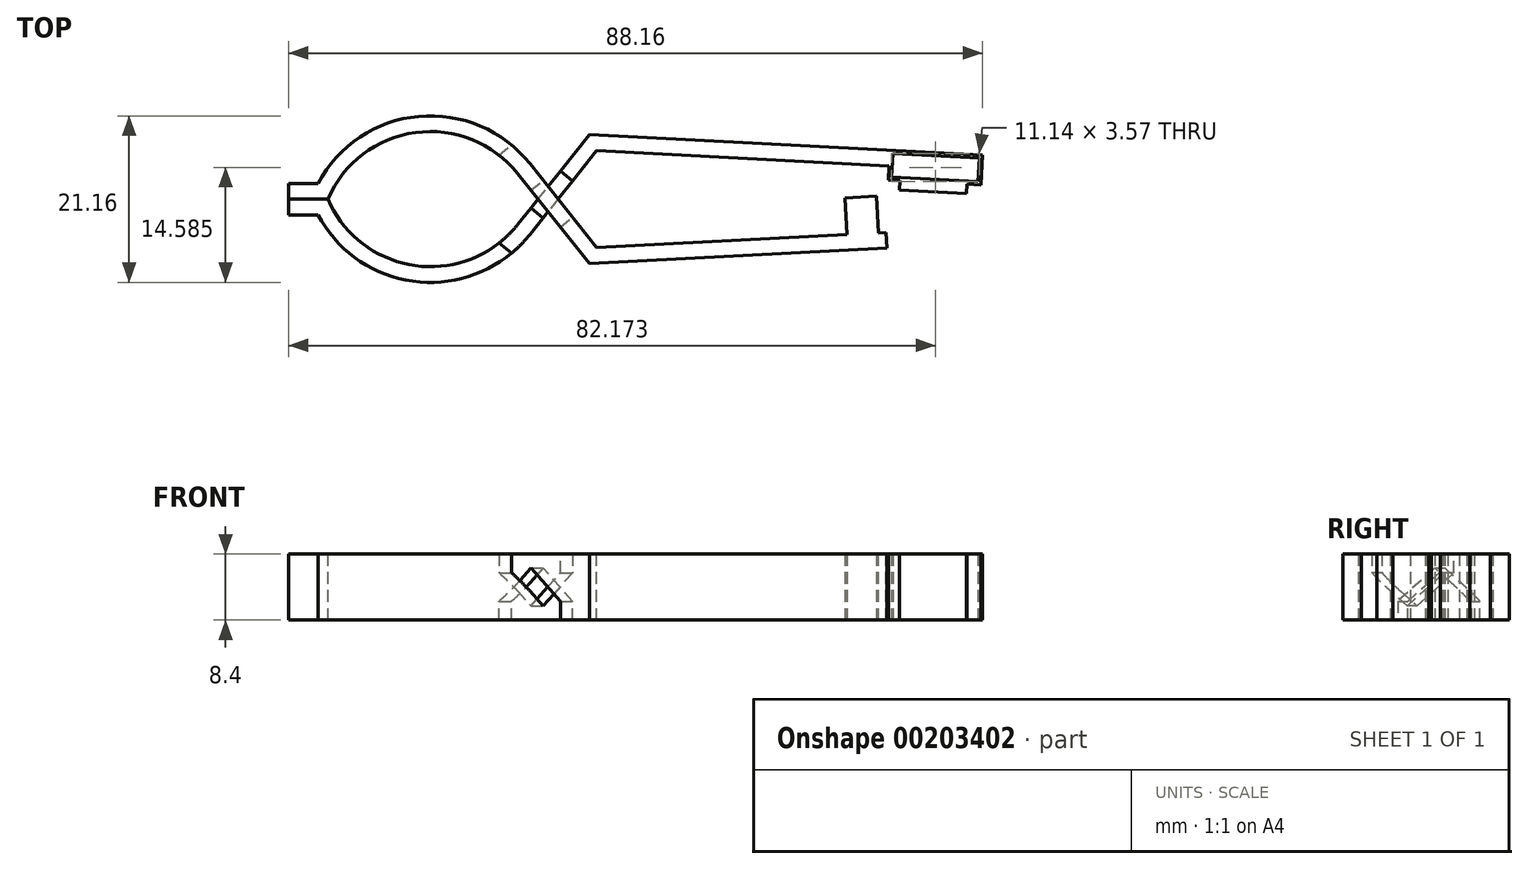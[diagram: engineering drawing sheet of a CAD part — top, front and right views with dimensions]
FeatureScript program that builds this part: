
annotation { "Feature Type Name" : "Feature", "Feature Type Description" : "" }
export const myFeature = defineFeature(function(context is Context, id is Id, definition is map)
    precondition{}
    {
        {
            var Q0;
            Q0=qCreatedBy(makeId("Top.planeOp"),FACE);
            var sketch = newSketch(context, id + "F0", { "sketchPlane" : qUnion([Q0])});
            skArc(sketch, "E0", {"start": v(-7.14, -2) * mm, "mid": v(5.65, -10.51) * mm, "end": v(19.78, -4.5) * mm});
            skArc(sketch, "E1", {"start": v(-5.88, 0) * mm, "mid": v(5.25, -8.45) * mm, "end": v(18.21, -3.25) * mm});
            skLineSegment(sketch, "E2.bottom", {"start": v(-10.88, -2) * mm, "end": v(-7.14, -2) * mm});
            skLineSegment(sketch, "E2.top", {"start": v(-10.88, 0) * mm, "end": v(-5.88, 0) * mm});
            skLineSegment(sketch, "E2.left", {"start": v(-10.88, -2) * mm, "end": v(-10.88, 0) * mm});
            skLineSegment(sketch, "E3", {"start": v(65.3, 2.42) * mm, "end": v(66.79, 2.34) * mm});
            skPoint(sketch, "E4.orphan", {"position": v(67.35, 0) * mm});
            skLineSegment(sketch, "E5.bottom", {"start": v(65.88, 5.8) * mm, "end": v(76.86, 5.22) * mm});
            skLineSegment(sketch, "E5.top", {"start": v(65.72, 2.8) * mm, "end": v(76.7, 2.22) * mm});
            skLineSegment(sketch, "E5.left", {"start": v(65.88, 5.8) * mm, "end": v(65.72, 2.8) * mm});
            skLineSegment(sketch, "E5.right", {"start": v(76.86, 5.22) * mm, "end": v(76.7, 2.22) * mm});
            skLineSegment(sketch, "E6", {"start": v(65.3, 2.42) * mm, "end": v(65.4, 4.21) * mm});
            skLineSegment(sketch, "E7", {"start": v(77.09, 1.8) * mm, "end": v(77.28, 5.6) * mm});
            skLineSegment(sketch, "E8", {"start": v(65.4, 4.21) * mm, "end": v(28.28, 6.16) * mm});
            skLineSegment(sketch, "E9", {"start": v(27.35, 8.21) * mm, "end": v(77.28, 5.6) * mm});
            skLineSegment(sketch, "E10", {"start": v(66.79, 2.34) * mm, "end": v(66.73, 1.14) * mm});
            skLineSegment(sketch, "E11", {"start": v(66.73, 1.14) * mm, "end": v(75.21, 0.7) * mm});
            skLineSegment(sketch, "E12", {"start": v(75.21, 0.7) * mm, "end": v(75.28, 1.9) * mm});
            skLineSegment(sketch, "E13.trimOffspring", {"start": v(75.28, 1.9) * mm, "end": v(77.09, 1.8) * mm});
            skLineSegment(sketch, "E14", {"start": v(19.78, -4.5) * mm, "end": v(28.28, 6.16) * mm});
            skLineSegment(sketch, "E15", {"start": v(27.35, 8.21) * mm, "end": v(18.21, -3.25) * mm});
            skSolve(sketch);
        }
        {
            var Q0;
            Q0 = qSketchRegion(id + "F0", true);
            extrude(context, id + "F1", {"entities" : qUnion([Q0]), "depth" : 4.2 * mm, "hasSecondDirection" : true, "secondDirectionOppositeDirection" : true, "secondDirectionDepth" : 4.2 * mm});
        }
        {
            var Q0;
            Q0=makeQuery(id+"F1.opExtrude","SWEPT_FACE",FACE,{"disambiguationData":[OSD([sQuery(id+"F0.wireOp",EDGE,"E14")])]});
            var sketch = newSketch(context, id + "F2", { "sketchPlane" : qUnion([Q0])});
            skLineSegment(sketch, "E16.bottom", {"start": v(5.52, 4.2) * mm, "end": v(17.52, 4.2) * mm});
            skLineSegment(sketch, "E16.left", {"start": v(5.52, 4.2) * mm, "end": v(5.52, 1.8) * mm});
            skLineSegment(sketch, "E16.right", {"start": v(17.52, 4.2) * mm, "end": v(17.52, 1.8) * mm});
            skLineSegment(sketch, "E17", {"start": v(17.52, 1.8) * mm, "end": v(11.52, -2.4) * mm});
            skLineSegment(sketch, "E18", {"start": v(11.52, -2.4) * mm, "end": v(5.52, 1.8) * mm});
            skSolve(sketch);
        }
        {
            var Q0;
            Q0 = qSketchRegion(id + "F2", true);
            extrude(context, id + "F3", {"entities" : qUnion([Q0]), "operationType" : NewBodyOperationType.REMOVE, "endBound" : BoundingType.UP_TO_NEXT, "oppositeDirection" : true, "depth" : 25 * mm});
        }
        {
            var Q0;
            Q0=makeQuery(id+"F1.opExtrude","SWEPT_BODY",BODY,{"disambiguationData":[OSD([sQuery(id+"F0.wireOp",EDGE,"FRPdRv6o-rn0N-uclI-ySpY-ZrcLyE1zcGhI.bottom"),sQuery(id+"F0.wireOp",EDGE,"FRPdRv6o-rn0N-uclI-ySpY-ZrcLyE1zcGhI.top"),sQuery(id+"F0.wireOp",EDGE,"FRPdRv6o-rn0N-uclI-ySpY-ZrcLyE1zcGhI.left"),sQuery(id+"F0.wireOp",EDGE,"FRPdRv6o-rn0N-uclI-ySpY-ZrcLyE1zcGhI.right"),sQuery(id+"F0.wireOp",EDGE,"mvS2vz2i-4XB0-zerM-x0aY-umKX9tXBcM6p.bottom"),sQuery(id+"F0.wireOp",EDGE,"mvS2vz2i-4XB0-zerM-x0aY-umKX9tXBcM6p.top"),sQuery(id+"F0.wireOp",EDGE,"E0"),sQuery(id+"F0.wireOp",EDGE,"E1"),sQuery(id+"F0.wireOp",EDGE,"E2.bottom"),sQuery(id+"F0.wireOp",EDGE,"E2.top"),sQuery(id+"F0.wireOp",EDGE,"E2.left")])]});
            var Q1;
            Q1=qCreatedBy(makeId("Top.planeOp"),FACE);
            mirror(context, id + "F4", {"entities" : qUnion([Q0]), "mirrorPlane" : qUnion([Q1])});
        }
        {
            var Q0;
            Q0=makeQuery(id+"F4.opPattern","COPY",BODY,{"derivedFrom":makeQuery(id+"F1.opExtrude","SWEPT_BODY",BODY,{"disambiguationData":[OSD([sQuery(id+"F0.wireOp",EDGE,"FRPdRv6o-rn0N-uclI-ySpY-ZrcLyE1zcGhI.bottom"),sQuery(id+"F0.wireOp",EDGE,"FRPdRv6o-rn0N-uclI-ySpY-ZrcLyE1zcGhI.top"),sQuery(id+"F0.wireOp",EDGE,"FRPdRv6o-rn0N-uclI-ySpY-ZrcLyE1zcGhI.left"),sQuery(id+"F0.wireOp",EDGE,"FRPdRv6o-rn0N-uclI-ySpY-ZrcLyE1zcGhI.right"),sQuery(id+"F0.wireOp",EDGE,"mvS2vz2i-4XB0-zerM-x0aY-umKX9tXBcM6p.bottom"),sQuery(id+"F0.wireOp",EDGE,"mvS2vz2i-4XB0-zerM-x0aY-umKX9tXBcM6p.top"),sQuery(id+"F0.wireOp",EDGE,"E0"),sQuery(id+"F0.wireOp",EDGE,"E1"),sQuery(id+"F0.wireOp",EDGE,"E2.bottom"),sQuery(id+"F0.wireOp",EDGE,"E2.top"),sQuery(id+"F0.wireOp",EDGE,"E2.left")])]}),"instanceName":"1"});
            var Q1;
            Q1=qCreatedBy(makeId("Front.planeOp"),FACE);
            mirror(context, id + "F5", {"entities" : qUnion([Q0]), "mirrorPlane" : qUnion([Q1])});
        }
        {
            var Q0;
            Q0=makeQuery(id+"F4.opPattern","COPY",BODY,{"derivedFrom":makeQuery(id+"F1.opExtrude","SWEPT_BODY",BODY,{"disambiguationData":[OSD([sQuery(id+"F0.wireOp",EDGE,"E0"),sQuery(id+"F0.wireOp",EDGE,"E1"),sQuery(id+"F0.wireOp",EDGE,"E2.bottom"),sQuery(id+"F0.wireOp",EDGE,"E2.top"),sQuery(id+"F0.wireOp",EDGE,"E2.left"),sQuery(id+"F0.wireOp",EDGE,"E3"),sQuery(id+"F0.wireOp",EDGE,"E5.bottom"),sQuery(id+"F0.wireOp",EDGE,"E5.top"),sQuery(id+"F0.wireOp",EDGE,"E5.left"),sQuery(id+"F0.wireOp",EDGE,"E5.right"),sQuery(id+"F0.wireOp",EDGE,"E6"),sQuery(id+"F0.wireOp",EDGE,"E7"),sQuery(id+"F0.wireOp",EDGE,"E8"),sQuery(id+"F0.wireOp",EDGE,"E9"),sQuery(id+"F0.wireOp",EDGE,"E10"),sQuery(id+"F0.wireOp",EDGE,"E11"),sQuery(id+"F0.wireOp",EDGE,"E12"),sQuery(id+"F0.wireOp",EDGE,"E13.trimOffspring"),sQuery(id+"F0.wireOp",EDGE,"E14"),sQuery(id+"F0.wireOp",EDGE,"E15")])]}),"instanceName":"1"});
            deleteBodies(context, id + "F6", {"entities" : qUnion([Q0])});
        }
        {
            var Q0;
            Q0=qCreatedBy(makeId("Top.planeOp"),FACE);
            var sketch = newSketch(context, id + "F7", { "sketchPlane" : qUnion([Q0])});
            skLineSegment(sketch, "E19", {"start": v(64.8, 0) * mm, "end": v(65.42, -10.98) * mm});
            skLineSegment(sketch, "E20", {"start": v(65.42, -10.98) * mm, "end": v(80.85, -9.18) * mm});
            skLineSegment(sketch, "E21", {"start": v(80.85, -9.18) * mm, "end": v(80.85, 0) * mm});
            skLineSegment(sketch, "E22", {"start": v(80.85, 0) * mm, "end": v(64.8, 0) * mm});
            skSolve(sketch);
        }
        {
            var Q0;
            Q0 = qSketchRegion(id + "F7", true);
            extrude(context, id + "F8", {"entities" : qUnion([Q0]), "operationType" : NewBodyOperationType.REMOVE, "endBound" : BoundingType.THROUGH_ALL, "oppositeDirection" : true, "depth" : 25 * mm, "hasSecondDirection" : true, "secondDirectionBound" : SecondDirectionBoundingType.THROUGH_ALL, "secondDirectionOppositeDirection" : false, "secondDirectionDepth" : 25 * mm});
        }
        {
            var Q0;
            Q0=qCreatedBy(makeId("Top.planeOp"),FACE);
            var sketch = newSketch(context, id + "F9", { "sketchPlane" : qUnion([Q0])});
            skLineSegment(sketch, "E23", {"start": v(59.79, 0.16) * mm, "end": v(60.14, -6.5) * mm});
            skLineSegment(sketch, "E24", {"start": v(60.14, -6.5) * mm, "end": v(64.13, -6.28) * mm});
            skLineSegment(sketch, "E25", {"start": v(64.13, -6.28) * mm, "end": v(63.78, 0.37) * mm});
            skLineSegment(sketch, "E26", {"start": v(63.78, 0.37) * mm, "end": v(59.79, 0.16) * mm});
            skPoint(sketch, "E27.orphan", {"position": v(59.8, 0) * mm});
            skSolve(sketch);
        }
        {
            var Q0;
            Q0 = qSketchRegion(id + "F9", true);
            var Q1;
            Q1=makeQuery(id+"F5.opPattern","COPY",FACE,{"derivedFrom":makeQuery(id+"F4.opPattern","COPY",FACE,{"derivedFrom":makeQuery(id+"F1.opExtrude","CAP_FACE",FACE,{"disambiguationData":[OSD([sQuery(id+"F0.wireOp",EDGE,"E0"),sQuery(id+"F0.wireOp",EDGE,"E1"),sQuery(id+"F0.wireOp",EDGE,"E2.bottom"),sQuery(id+"F0.wireOp",EDGE,"E2.top"),sQuery(id+"F0.wireOp",EDGE,"E2.left"),sQuery(id+"F0.wireOp",EDGE,"E3"),sQuery(id+"F0.wireOp",EDGE,"E5.bottom"),sQuery(id+"F0.wireOp",EDGE,"E5.top"),sQuery(id+"F0.wireOp",EDGE,"E5.left"),sQuery(id+"F0.wireOp",EDGE,"E5.right"),sQuery(id+"F0.wireOp",EDGE,"E6"),sQuery(id+"F0.wireOp",EDGE,"E7"),sQuery(id+"F0.wireOp",EDGE,"E8"),sQuery(id+"F0.wireOp",EDGE,"E9"),sQuery(id+"F0.wireOp",EDGE,"E10"),sQuery(id+"F0.wireOp",EDGE,"E11"),sQuery(id+"F0.wireOp",EDGE,"E12"),sQuery(id+"F0.wireOp",EDGE,"E13.trimOffspring"),sQuery(id+"F0.wireOp",EDGE,"E14"),sQuery(id+"F0.wireOp",EDGE,"E15")])],"isStart":true}),"instanceName":"1"}),"instanceName":"1"});
            var Q2;
            {var subQ0=sQuery(id+"F0.wireOp",EDGE,"E10");var subQ1=sQuery(id+"F0.wireOp",EDGE,"E9");var subQ2=sQuery(id+"F0.wireOp",EDGE,"E8");var subQ3=sQuery(id+"F0.wireOp",EDGE,"E7");var subQ4=sQuery(id+"F0.wireOp",EDGE,"E6");var subQ5=sQuery(id+"F0.wireOp",EDGE,"E5.right");var subQ6=sQuery(id+"F0.wireOp",EDGE,"E3");var subQ7=sQuery(id+"F0.wireOp",EDGE,"E5.bottom");var subQ8=sQuery(id+"F0.wireOp",EDGE,"E5.top");var subQ9=sQuery(id+"F0.wireOp",EDGE,"E5.left");var subQ10=sQuery(id+"F0.wireOp",EDGE,"E11");var subQ11=sQuery(id+"F0.wireOp",EDGE,"E12");var subQ12=sQuery(id+"F0.wireOp",EDGE,"E13.trimOffspring");var subQ13=sQuery(id+"F0.wireOp",EDGE,"E14");var subQ14=sQuery(id+"F0.wireOp",EDGE,"E15");Q2=makeQuery(id+"F5.opPattern","COPY",FACE,{"derivedFrom":makeQuery(id+"F4.opPattern","COPY",FACE,{"derivedFrom":makeQuery(id+"F3.boolean.opBoolean","SPLIT",FACE,{"disambiguationData":[TD([makeQuery(id+"F1.opExtrude","SWEPT_FACE",FACE,{"disambiguationData":[OSD([subQ6])]})])],"derivedFrom":makeQuery(id+"F1.opExtrude","CAP_FACE",FACE,{"disambiguationData":[OSD([sQuery(id+"F0.wireOp",EDGE,"E0"),sQuery(id+"F0.wireOp",EDGE,"E1"),sQuery(id+"F0.wireOp",EDGE,"E2.bottom"),sQuery(id+"F0.wireOp",EDGE,"E2.top"),sQuery(id+"F0.wireOp",EDGE,"E2.left"),subQ6,subQ7,subQ8,subQ9,subQ5,subQ4,subQ3,subQ2,subQ1,subQ0,subQ10,subQ11,subQ12,subQ13,subQ14])],"isStart":false})}),"instanceName":"1"}),"instanceName":"1"});}
            extrude(context, id + "F10", {"entities" : qUnion([Q0]), "operationType" : NewBodyOperationType.ADD, "endBound" : BoundingType.UP_TO_SURFACE, "endBoundEntityFace" : qUnion([Q1]), "depth" : 25 * mm, "hasSecondDirection" : true, "secondDirectionBound" : SecondDirectionBoundingType.UP_TO_SURFACE, "secondDirectionOppositeDirection" : true, "secondDirectionBoundEntityFace" : qUnion([Q2]), "secondDirectionDepth" : 25 * mm});
        }
    });
